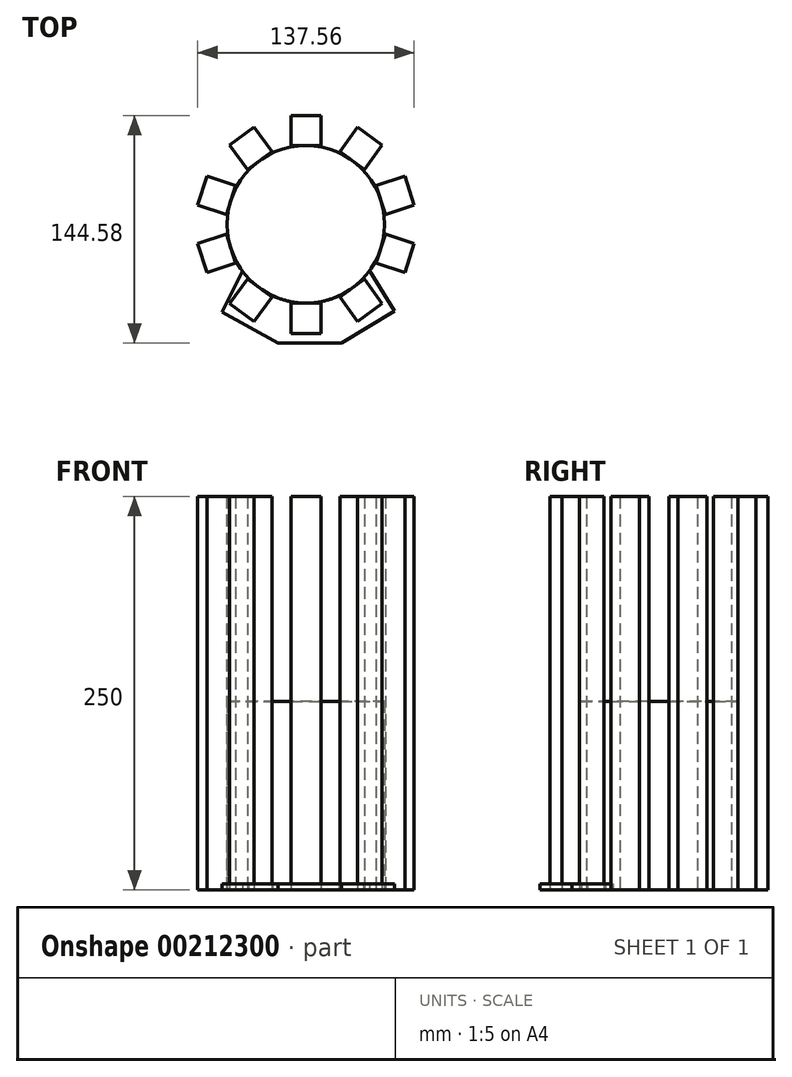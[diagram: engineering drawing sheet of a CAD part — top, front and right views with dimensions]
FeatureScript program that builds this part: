
annotation { "Feature Type Name" : "Feature", "Feature Type Description" : "" }
export const myFeature = defineFeature(function(context is Context, id is Id, definition is map)
    precondition{}
    {
        {
            var Q0;
            Q0=qCreatedBy(makeId("Top.planeOp"),FACE);
            var sketch = newSketch(context, id + "F0", { "sketchPlane" : qUnion([Q0])});
            skCircle(sketch, "E0", {"center": v(0, 0) * mm, "radius": 50 * mm});
            skLineSegment(sketch, "E1.bottom", {"start": v(-9.6, -50) * mm, "end": v(9.6, -50) * mm});
            skLineSegment(sketch, "E1.top", {"start": v(-9.6, -69.2) * mm, "end": v(9.6, -69.2) * mm});
            skLineSegment(sketch, "E1.left", {"start": v(-9.6, -50) * mm, "end": v(-9.6, -69.2) * mm});
            skLineSegment(sketch, "E1.right", {"start": v(9.6, -50) * mm, "end": v(9.6, -69.2) * mm});
            skLineSegment(sketch, "E2", {"start": v(0, 0) * mm, "end": v(0, -93.47) * mm, "construction": true});
            skPoint(sketch, "E3", {"position": v(0, -50) * mm});
            skLineSegment(sketch, "E4.1.0", {"start": v(21.62, -46.1) * mm, "end": v(37.16, -34.8) * mm});
            skLineSegment(sketch, "E4.1.1", {"start": v(37.16, -34.8) * mm, "end": v(48.44, -50.34) * mm});
            skLineSegment(sketch, "E4.1.2", {"start": v(32.9, -61.63) * mm, "end": v(48.44, -50.34) * mm});
            skLineSegment(sketch, "E4.1.3", {"start": v(21.62, -46.1) * mm, "end": v(32.9, -61.63) * mm});
            skLineSegment(sketch, "E4.2.0", {"start": v(44.59, -24.58) * mm, "end": v(50.52, -6.32) * mm});
            skLineSegment(sketch, "E4.2.1", {"start": v(50.52, -6.32) * mm, "end": v(68.78, -12.25) * mm});
            skLineSegment(sketch, "E4.2.2", {"start": v(62.85, -30.51) * mm, "end": v(68.78, -12.25) * mm});
            skLineSegment(sketch, "E4.2.3", {"start": v(44.59, -24.58) * mm, "end": v(62.85, -30.51) * mm});
            skLineSegment(sketch, "E4.3.0", {"start": v(50.52, 6.32) * mm, "end": v(44.59, 24.58) * mm});
            skLineSegment(sketch, "E4.3.1", {"start": v(44.59, 24.58) * mm, "end": v(62.85, 30.51) * mm});
            skLineSegment(sketch, "E4.3.2", {"start": v(68.78, 12.25) * mm, "end": v(62.85, 30.51) * mm});
            skLineSegment(sketch, "E4.3.3", {"start": v(50.52, 6.32) * mm, "end": v(68.78, 12.25) * mm});
            skLineSegment(sketch, "E4.4.0", {"start": v(37.16, 34.8) * mm, "end": v(21.62, 46.1) * mm});
            skLineSegment(sketch, "E4.4.1", {"start": v(21.62, 46.1) * mm, "end": v(32.9, 61.63) * mm});
            skLineSegment(sketch, "E4.4.2", {"start": v(48.44, 50.34) * mm, "end": v(32.9, 61.63) * mm});
            skLineSegment(sketch, "E4.4.3", {"start": v(37.16, 34.8) * mm, "end": v(48.44, 50.34) * mm});
            skLineSegment(sketch, "E4.5.0", {"start": v(9.6, 50) * mm, "end": v(-9.6, 50) * mm});
            skLineSegment(sketch, "E4.5.1", {"start": v(-9.6, 50) * mm, "end": v(-9.6, 69.2) * mm});
            skLineSegment(sketch, "E4.5.2", {"start": v(9.6, 69.2) * mm, "end": v(-9.6, 69.2) * mm});
            skLineSegment(sketch, "E4.5.3", {"start": v(9.6, 50) * mm, "end": v(9.6, 69.2) * mm});
            skLineSegment(sketch, "E4.6.0", {"start": v(-21.62, 46.1) * mm, "end": v(-37.16, 34.8) * mm});
            skLineSegment(sketch, "E4.6.1", {"start": v(-37.16, 34.8) * mm, "end": v(-48.44, 50.34) * mm});
            skLineSegment(sketch, "E4.6.2", {"start": v(-32.9, 61.63) * mm, "end": v(-48.44, 50.34) * mm});
            skLineSegment(sketch, "E4.6.3", {"start": v(-21.62, 46.1) * mm, "end": v(-32.9, 61.63) * mm});
            skLineSegment(sketch, "E4.7.0", {"start": v(-44.59, 24.58) * mm, "end": v(-50.52, 6.32) * mm});
            skLineSegment(sketch, "E4.7.1", {"start": v(-50.52, 6.32) * mm, "end": v(-68.78, 12.25) * mm});
            skLineSegment(sketch, "E4.7.2", {"start": v(-62.85, 30.51) * mm, "end": v(-68.78, 12.25) * mm});
            skLineSegment(sketch, "E4.7.3", {"start": v(-44.59, 24.58) * mm, "end": v(-62.85, 30.51) * mm});
            skLineSegment(sketch, "E4.8.0", {"start": v(-50.52, -6.32) * mm, "end": v(-44.59, -24.58) * mm});
            skLineSegment(sketch, "E4.8.1", {"start": v(-44.59, -24.58) * mm, "end": v(-62.85, -30.51) * mm});
            skLineSegment(sketch, "E4.8.2", {"start": v(-68.78, -12.25) * mm, "end": v(-62.85, -30.51) * mm});
            skLineSegment(sketch, "E4.8.3", {"start": v(-50.52, -6.32) * mm, "end": v(-68.78, -12.25) * mm});
            skLineSegment(sketch, "E4.9.0", {"start": v(-37.16, -34.8) * mm, "end": v(-21.62, -46.1) * mm});
            skLineSegment(sketch, "E4.9.1", {"start": v(-21.62, -46.1) * mm, "end": v(-32.9, -61.63) * mm});
            skLineSegment(sketch, "E4.9.2", {"start": v(-48.44, -50.34) * mm, "end": v(-32.9, -61.63) * mm});
            skLineSegment(sketch, "E4.9.3", {"start": v(-37.16, -34.8) * mm, "end": v(-48.44, -50.34) * mm});
            skSolve(sketch);
        }
        {
            var Q0;
            {var subQ0=sQuery(id+"F0.wireOp",EDGE,"E0");var subQ6=makeQuery(id+"F0.imprint","INTERSECT",VERTEX,{"derivedFrom":[subQ0,sQuery(id+"F0.wireOp",EDGE,"E4.4.0")]});Q0=makeQuery(id+"F0.imprint","IMPRINT",FACE,{"disambiguationData":[TD([[makeQuery(id+"F0.imprint","IMPRINT",EDGE,{"disambiguationData":[TD([[subQ6,1.0]])],"derivedFrom":subQ0}),1.0]])]});}
            extrude(context, id + "F1", {"entities" : qUnion([Q0]), "depth" : 120 * mm});
        }
        {
            var Q0;
            {var subQ0=sQuery(id+"F0.wireOp",EDGE,"E4.9.1");Q0=makeQuery(id+"F0.imprint","IMPRINT",FACE,{"disambiguationData":[TD([[makeQuery(id+"F0.imprint","IMPRINT",EDGE,{"derivedFrom":subQ0}),-1.0]])]});}
            var Q1;
            {var subQ0=sQuery(id+"F0.wireOp",EDGE,"E4.8.1");Q1=makeQuery(id+"F0.imprint","IMPRINT",FACE,{"disambiguationData":[TD([[makeQuery(id+"F0.imprint","IMPRINT",EDGE,{"derivedFrom":subQ0}),-1.0]])]});}
            var Q2;
            Q2=makeQuery(id+"F0.imprint","IMPRINT",FACE,{"disambiguationData":[TD([[makeQuery(id+"F0.imprint","IMPRINT",EDGE,{"derivedFrom":sQuery(id+"F0.wireOp",EDGE,"E1.top")}),1.0]])]});
            var Q3;
            {var subQ0=sQuery(id+"F0.wireOp",EDGE,"E4.1.1");Q3=makeQuery(id+"F0.imprint","IMPRINT",FACE,{"disambiguationData":[TD([[makeQuery(id+"F0.imprint","IMPRINT",EDGE,{"derivedFrom":subQ0}),-1.0]])]});}
            var Q4;
            {var subQ0=sQuery(id+"F0.wireOp",EDGE,"E4.2.1");Q4=makeQuery(id+"F0.imprint","IMPRINT",FACE,{"disambiguationData":[TD([[makeQuery(id+"F0.imprint","IMPRINT",EDGE,{"derivedFrom":subQ0}),-1.0]])]});}
            var Q5;
            {var subQ0=sQuery(id+"F0.wireOp",EDGE,"E4.3.1");Q5=makeQuery(id+"F0.imprint","IMPRINT",FACE,{"disambiguationData":[TD([[makeQuery(id+"F0.imprint","IMPRINT",EDGE,{"derivedFrom":subQ0}),-1.0]])]});}
            var Q6;
            {var subQ0=sQuery(id+"F0.wireOp",EDGE,"E4.4.1");Q6=makeQuery(id+"F0.imprint","IMPRINT",FACE,{"disambiguationData":[TD([[makeQuery(id+"F0.imprint","IMPRINT",EDGE,{"derivedFrom":subQ0}),-1.0]])]});}
            var Q7;
            {var subQ0=sQuery(id+"F0.wireOp",EDGE,"E4.5.1");Q7=makeQuery(id+"F0.imprint","IMPRINT",FACE,{"disambiguationData":[TD([[makeQuery(id+"F0.imprint","IMPRINT",EDGE,{"derivedFrom":subQ0}),-1.0]])]});}
            var Q8;
            {var subQ0=sQuery(id+"F0.wireOp",EDGE,"E4.6.1");Q8=makeQuery(id+"F0.imprint","IMPRINT",FACE,{"disambiguationData":[TD([[makeQuery(id+"F0.imprint","IMPRINT",EDGE,{"derivedFrom":subQ0}),-1.0]])]});}
            var Q9;
            {var subQ0=sQuery(id+"F0.wireOp",EDGE,"E4.7.1");Q9=makeQuery(id+"F0.imprint","IMPRINT",FACE,{"disambiguationData":[TD([[makeQuery(id+"F0.imprint","IMPRINT",EDGE,{"derivedFrom":subQ0}),-1.0]])]});}
            extrude(context, id + "F2", {"entities" : qUnion([Q0, Q1, Q2, Q3, Q4, Q5, Q6, Q7, Q8, Q9]), "operationType" : NewBodyOperationType.ADD, "depth" : 250 * mm});
        }
        {
            var Q0;
            Q0=qCreatedBy(makeId("Top.planeOp"),FACE);
            var sketch = newSketch(context, id + "F3", { "sketchPlane" : qUnion([Q0])});
            skCircle(sketch, "E5.0", {"center": v(0, 0) * mm, "radius": 50 * mm});
            skLineSegment(sketch, "E5.1.1", {"start": v(-37.16, -34.8) * mm, "end": v(-48.44, -50.34) * mm});
            skLineSegment(sketch, "E5.1.2", {"start": v(-48.44, -50.34) * mm, "end": v(-32.9, -61.63) * mm});
            skLineSegment(sketch, "E5.1.3", {"start": v(-32.9, -61.63) * mm, "end": v(-21.62, -46.1) * mm});
            skLineSegment(sketch, "E5.2.0", {"start": v(-9.6, -50) * mm, "end": v(-9.6, -69.2) * mm});
            skLineSegment(sketch, "E5.2.1", {"start": v(-9.6, -69.2) * mm, "end": v(9.6, -69.2) * mm});
            skLineSegment(sketch, "E5.2.2", {"start": v(9.6, -69.2) * mm, "end": v(9.6, -50) * mm});
            skLineSegment(sketch, "E5.2.3", {"start": v(9.6, -50) * mm, "end": v(-9.6, -50) * mm});
            skLineSegment(sketch, "E5.3.0", {"start": v(37.16, -34.8) * mm, "end": v(21.62, -46.1) * mm});
            skLineSegment(sketch, "E5.3.1", {"start": v(21.62, -46.1) * mm, "end": v(32.9, -61.63) * mm});
            skLineSegment(sketch, "E5.3.2", {"start": v(32.9, -61.63) * mm, "end": v(48.44, -50.34) * mm});
            skLineSegment(sketch, "E5.3.3", {"start": v(48.44, -50.34) * mm, "end": v(37.16, -34.8) * mm});
            skLineSegment(sketch, "E6", {"start": v(-17.61, -75.38) * mm, "end": v(22.64, -75.38) * mm});
            skLineSegment(sketch, "E7", {"start": v(56.16, -55.08) * mm, "end": v(40.54, -29.27) * mm});
            skLineSegment(sketch, "E8", {"start": v(-40.33, -29.56) * mm, "end": v(-53.25, -55.58) * mm});
            skLineSegment(sketch, "E9", {"start": v(-53.25, -55.58) * mm, "end": v(-17.61, -75.38) * mm});
            skLineSegment(sketch, "E10", {"start": v(22.64, -75.38) * mm, "end": v(56.16, -55.08) * mm});
            skLineSegment(sketch, "E11", {"start": v(-37.16, -34.8) * mm, "end": v(-36.54, -34.13) * mm});
            skLineSegment(sketch, "E12", {"start": v(-36.54, -34.13) * mm, "end": v(-40.33, -29.56) * mm});
            skPoint(sketch, "E13.end.orphan", {"position": v(-37.16, -23.18) * mm});
            skPoint(sketch, "E14.end.orphan", {"position": v(0, -50) * mm});
            skLineSegment(sketch, "E15", {"start": v(37.16, -34.8) * mm, "end": v(36.6, -34.06) * mm});
            skLineSegment(sketch, "E16", {"start": v(36.6, -34.06) * mm, "end": v(40.54, -29.27) * mm});
            skLineSegment(sketch, "E17", {"start": v(-40.33, -29.56) * mm, "end": v(40.54, -29.27) * mm});
            skArc(sketch, "E18", {"start": v(21.67, -46.17) * mm, "mid": v(29.98, -41.26) * mm, "end": v(37.2, -34.88) * mm});
            skLineSegment(sketch, "E19", {"start": v(21.62, -46.1) * mm, "end": v(21.08, -45.34) * mm});
            skLineSegment(sketch, "E20", {"start": v(9.6, -50) * mm, "end": v(9.6, -46.64) * mm});
            skLineSegment(sketch, "E21", {"start": v(-9.6, -50) * mm, "end": v(-9.6, -46.46) * mm});
            skLineSegment(sketch, "E22", {"start": v(-21.62, -46.1) * mm, "end": v(-21.08, -45.34) * mm});
            skArc(sketch, "E23.trimOffspring", {"start": v(41.1, -30.2) * mm, "mid": v(-0.23, 51) * mm, "end": v(-40.83, -30.57) * mm});
            skArc(sketch, "E24.trimOffspring", {"start": v(-37.2, -34.88) * mm, "mid": v(-29.98, -41.26) * mm, "end": v(-21.67, -46.17) * mm});
            skSolve(sketch);
        }
        {
            var Q0;
            {var subQ1=sQuery(id+"F3.wireOp",EDGE,"E5.1.2");Q0=makeQuery(id+"F3.imprint","IMPRINT",FACE,{"disambiguationData":[TD([[makeQuery(id+"F3.imprint","IMPRINT",EDGE,{"derivedFrom":subQ1}),-1.0]])]});}
            var Q1;
            {var subQ0=sQuery(id+"F3.wireOp",EDGE,"VQ4EVVbP-fSg5-dSDK-XAsj-Fd4XgZ4hKzau");Q1=makeQuery(id+"F3.imprint","IMPRINT",FACE,{"disambiguationData":[TD([[makeQuery(id+"F3.imprint","IMPRINT",EDGE,{"derivedFrom":subQ0}),1.0]])]});}
            var Q2;
            {var subQ3=sQuery(id+"F3.wireOp",EDGE,"4Wn8HV2Q-aeVr-9PkN-2usv-KW3yOWRwW1gy");Q2=makeQuery(id+"F3.imprint","IMPRINT",FACE,{"disambiguationData":[TD([[makeQuery(id+"F3.imprint","IMPRINT",EDGE,{"derivedFrom":subQ3}),1.0]])]});}
            var Q3;
            {var subQ0=sQuery(id+"F3.wireOp",EDGE,"E11");Q3=makeQuery(id+"F3.imprint","IMPRINT",FACE,{"disambiguationData":[TD([[makeQuery(id+"F3.imprint","IMPRINT",EDGE,{"derivedFrom":subQ0}),1.0]])]});}
            var Q4;
            {var subQ0=sQuery(id+"F3.wireOp",EDGE,"E15");Q4=makeQuery(id+"F3.imprint","IMPRINT",FACE,{"disambiguationData":[TD([[makeQuery(id+"F3.imprint","IMPRINT",EDGE,{"derivedFrom":subQ0}),-1.0]])]});}
            extrude(context, id + "F4", {"entities" : qUnion([Q0, Q1, Q2, Q3, Q4]), "depth" : 4 * mm});
        }
    });
